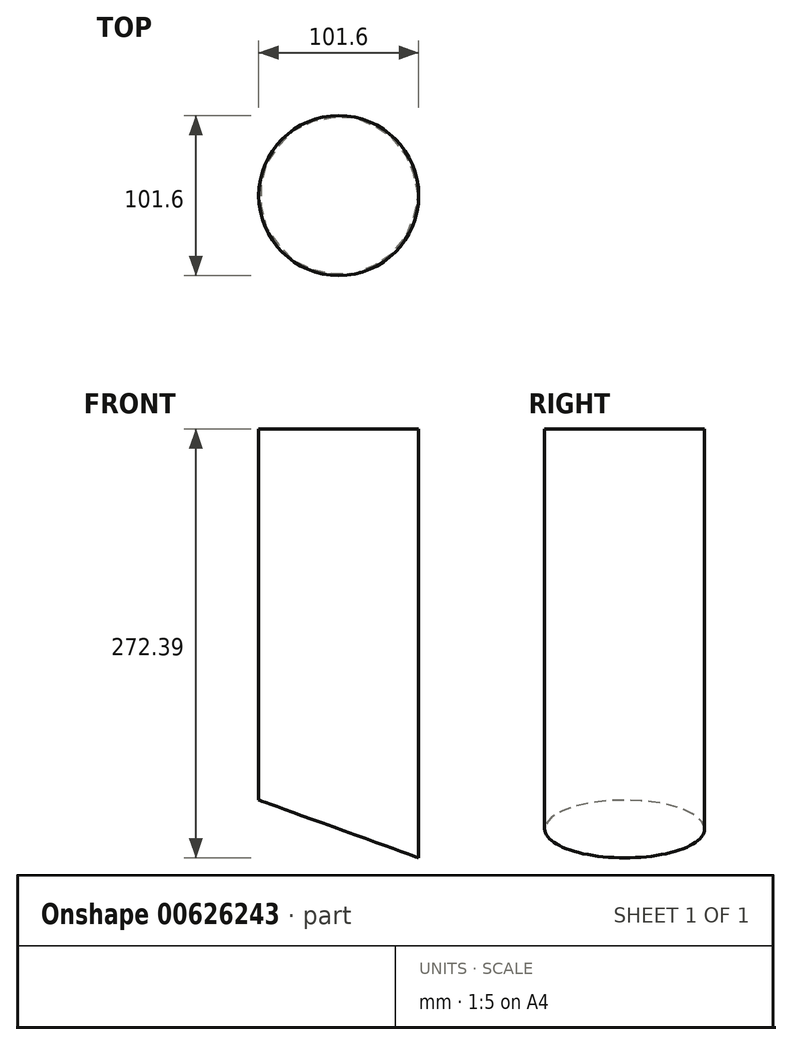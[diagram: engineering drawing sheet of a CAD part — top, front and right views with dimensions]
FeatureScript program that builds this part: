
annotation { "Feature Type Name" : "Feature", "Feature Type Description" : "" }
export const myFeature = defineFeature(function(context is Context, id is Id, definition is map)
    precondition{}
    {
        {
            var Q0;
            Q0=qCreatedBy(makeId("Top.planeOp"),FACE);
            var sketch = newSketch(context, id + "F0", { "sketchPlane" : qUnion([Q0])});
            skCircle(sketch, "E0", {"center": v(0, 0) * mm, "radius": 50.8 * mm});
            skSolve(sketch);
        }
        {
            var Q0;
            Q0 = qSketchRegion(id + "F0", true);
            extrude(context, id + "F1", {"entities" : qUnion([Q0]), "depth" : 254 * mm, "offsetDistance" : 25.4 * mm, "hasSecondDirection" : true, "secondDirectionOppositeDirection" : true, "secondDirectionDepth" : 254 * mm});
        }
        {
            var Q0;
            Q0=qCreatedBy(makeId("Front.planeOp"),FACE);
            var sketch = newSketch(context, id + "F2", { "sketchPlane" : qUnion([Q0])});
            skLineSegment(sketch, "E1", {"start": v(0, 0) * mm, "end": v(-134.69, 48.76) * mm});
            skLineSegment(sketch, "E2", {"start": v(-134.69, 48.76) * mm, "end": v(-124.86, -294.27) * mm});
            skLineSegment(sketch, "E3", {"start": v(-124.86, -294.27) * mm, "end": v(92.13, -299.89) * mm});
            skLineSegment(sketch, "E4", {"start": v(92.13, -299.89) * mm, "end": v(122.75, -44.43) * mm});
            skLineSegment(sketch, "E5", {"start": v(122.75, -44.43) * mm, "end": v(0, 0) * mm});
            skSolve(sketch);
        }
        {
            var Q0;
            Q0 = qSketchRegion(id + "F2", true);
            extrude(context, id + "F3", {"entities" : qUnion([Q0]), "operationType" : NewBodyOperationType.REMOVE, "endBound" : BoundingType.THROUGH_ALL, "oppositeDirection" : true, "depth" : 25.4 * mm, "offsetDistance" : 25.4 * mm, "hasSecondDirection" : true, "secondDirectionBound" : SecondDirectionBoundingType.THROUGH_ALL, "secondDirectionOppositeDirection" : false, "secondDirectionDepth" : 25.4 * mm});
        }
    });
